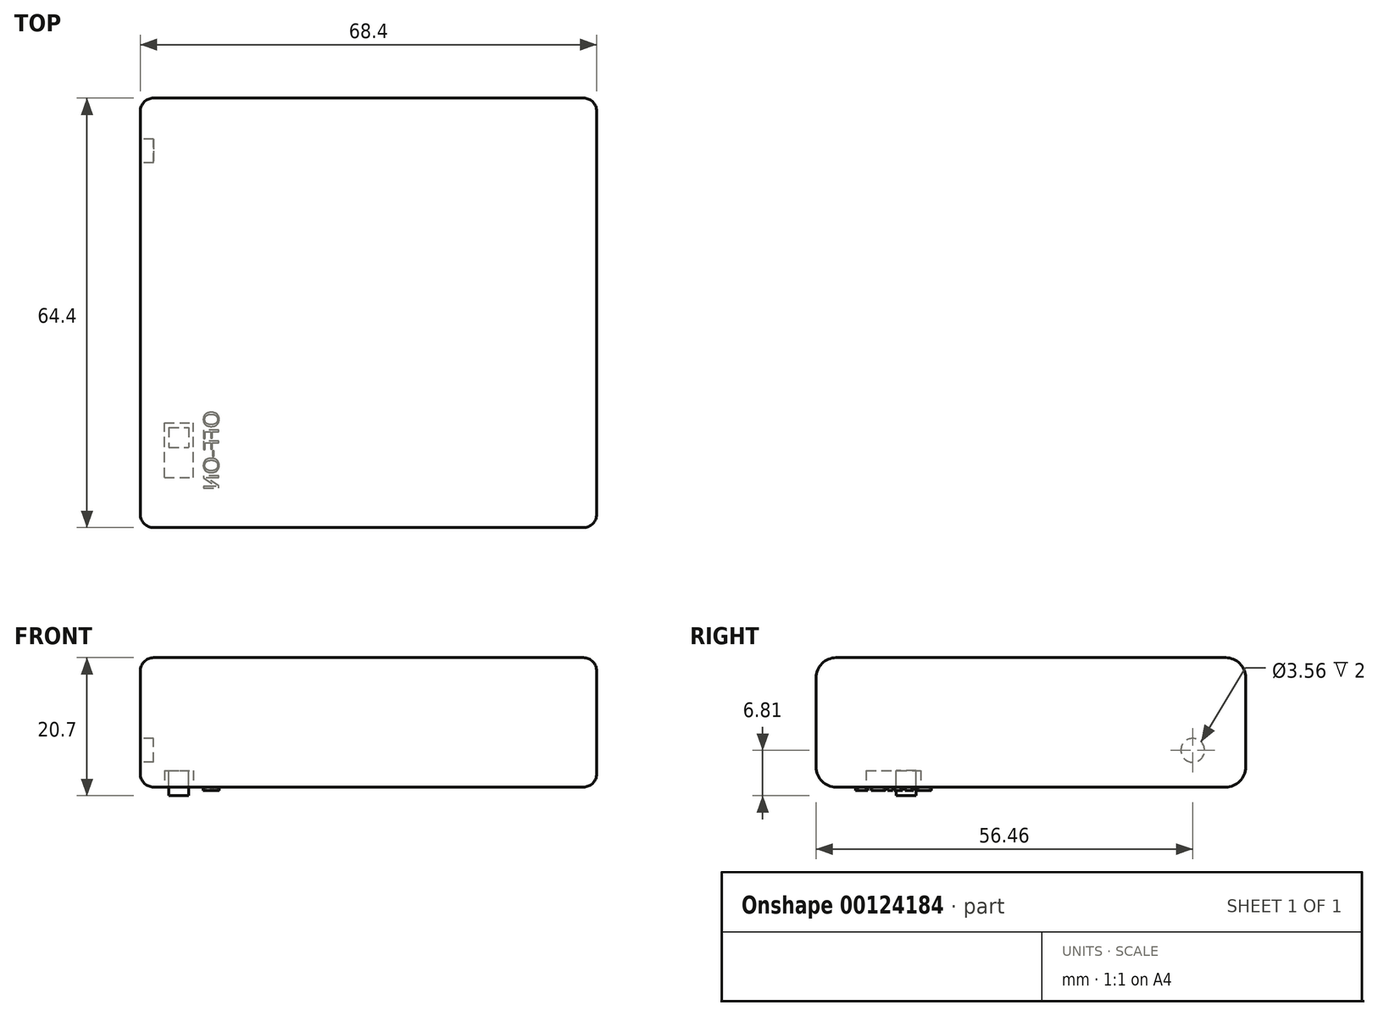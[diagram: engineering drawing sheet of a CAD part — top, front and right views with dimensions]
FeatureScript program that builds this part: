
annotation { "Feature Type Name" : "Feature", "Feature Type Description" : "" }
export const myFeature = defineFeature(function(context is Context, id is Id, definition is map)
    precondition{}
    {
        {
            var Q0;
            Q0=qCreatedBy(makeId("Top.planeOp"),FACE);
            var sketch = newSketch(context, id + "F0", { "sketchPlane" : qUnion([Q0])});
            skLineSegment(sketch, "E0.bottom", {"start": v(32.2, 34.2) * mm, "end": v(-32.2, 34.2) * mm});
            skLineSegment(sketch, "E0.top", {"start": v(32.2, -34.2) * mm, "end": v(-32.2, -34.2) * mm});
            skLineSegment(sketch, "E0.left", {"start": v(32.2, 34.2) * mm, "end": v(32.2, -34.2) * mm});
            skLineSegment(sketch, "E0.right", {"start": v(-32.2, 34.2) * mm, "end": v(-32.2, -34.2) * mm});
            skPoint(sketch, "E0.middle", {"position": v(0, 0) * mm});
            skSolve(sketch);
        }
        {
            var Q0;
            Q0 = qSketchRegion(id + "F0", true);
            extrude(context, id + "F1", {"entities" : qUnion([Q0]), "depth" : 19.4 * mm});
        }
        {
            var Q0;
            Q0=makeQuery(id+"F1.opExtrude","CAP_EDGE",EDGE,{"disambiguationData":[OSD([sQuery(id+"F0.wireOp",EDGE,"E0.right")])],"isStart":false});
            var Q1;
            Q1=makeQuery(id+"F1.opExtrude","CAP_EDGE",EDGE,{"disambiguationData":[OSD([sQuery(id+"F0.wireOp",EDGE,"E0.left")])],"isStart":false});
            var Q2;
            Q2=makeQuery(id+"F1.opExtrude","CAP_EDGE",EDGE,{"disambiguationData":[OSD([sQuery(id+"F0.wireOp",EDGE,"E0.left")])],"isStart":true});
            var Q3;
            Q3=makeQuery(id+"F1.opExtrude","CAP_EDGE",EDGE,{"disambiguationData":[OSD([sQuery(id+"F0.wireOp",EDGE,"E0.right")])],"isStart":true});
            fillet(context, id + "F2", {"entities" : qUnion([Q0, Q1, Q2, Q3]), "radius" : 3 * mm, "tangentPropagation" : true, "allowEdgeOverflow" : false});
        }
        {
            var Q0;
            Q0=makeQuery(id+"F1.opExtrude","SWEPT_FACE",FACE,{"disambiguationData":[OSD([sQuery(id+"F0.wireOp",EDGE,"E0.top")])]});
            var Q1;
            Q1=makeQuery(id+"F1.opExtrude","SWEPT_FACE",FACE,{"disambiguationData":[OSD([sQuery(id+"F0.wireOp",EDGE,"E0.bottom")])]});
            fillet(context, id + "F3", {"entities" : qUnion([Q0, Q1]), "radius" : 2 * mm, "tangentPropagation" : true, "allowEdgeOverflow" : false});
        }
        {
            var Q0;
            Q0=makeQuery(id+"F1.opExtrude","CAP_FACE",FACE,{"disambiguationData":[OSD([sQuery(id+"F0.wireOp",EDGE,"E0.bottom"),sQuery(id+"F0.wireOp",EDGE,"E0.top"),sQuery(id+"F0.wireOp",EDGE,"E0.left"),sQuery(id+"F0.wireOp",EDGE,"E0.right")])],"isStart":false});
            var sketch = newSketch(context, id + "F4", { "sketchPlane" : qUnion([Q0])});
            skLineSegment(sketch, "E1.bottom", {"start": v(24.7, 30.6) * mm, "end": v(16.5, 30.6) * mm});
            skLineSegment(sketch, "E1.top", {"start": v(24.7, 26.25) * mm, "end": v(16.5, 26.25) * mm});
            skLineSegment(sketch, "E1.left", {"start": v(24.7, 30.6) * mm, "end": v(24.7, 26.25) * mm});
            skLineSegment(sketch, "E1.right", {"start": v(16.5, 30.6) * mm, "end": v(16.5, 26.25) * mm});
            skSolve(sketch);
        }
        {
            var Q0;
            Q0 = qSketchRegion(id + "F4", true);
            extrude(context, id + "F5", {"entities" : qUnion([Q0]), "operationType" : NewBodyOperationType.REMOVE, "oppositeDirection" : true, "depth" : 2.5 * mm});
        }
        {
            var Q0;
            Q0=makeQuery(id+"F5.boolean.opBoolean","COPY",FACE,{"derivedFrom":makeQuery(id+"F5.opExtrude","CAP_FACE",FACE,{"disambiguationData":[OSD([sQuery(id+"F4.wireOp",EDGE,"E1.bottom"),sQuery(id+"F4.wireOp",EDGE,"E1.top"),sQuery(id+"F4.wireOp",EDGE,"E1.left"),sQuery(id+"F4.wireOp",EDGE,"E1.right")])],"isStart":false})});
            var sketch = newSketch(context, id + "F6", { "sketchPlane" : qUnion([Q0])});
            skLineSegment(sketch, "E2", {"start": v(16.5, 28.43) * mm, "end": v(24.7, 28.43) * mm, "construction": true});
            skLineSegment(sketch, "E3.bottom", {"start": v(17.18, 29.92) * mm, "end": v(20.18, 29.92) * mm});
            skLineSegment(sketch, "E3.top", {"start": v(17.18, 26.92) * mm, "end": v(20.18, 26.92) * mm});
            skLineSegment(sketch, "E3.left", {"start": v(17.18, 29.92) * mm, "end": v(17.18, 26.92) * mm});
            skLineSegment(sketch, "E3.right", {"start": v(20.18, 29.92) * mm, "end": v(20.18, 26.92) * mm});
            skPoint(sketch, "E3.middle", {"position": v(18.68, 28.42) * mm});
            skSolve(sketch);
        }
        {
            var Q0;
            Q0 = qSketchRegion(id + "F6", true);
            extrude(context, id + "F7", {"entities" : qUnion([Q0]), "operationType" : NewBodyOperationType.ADD, "depth" : (1.3 + 2.5) * mm});
        }
        {
            var Q0;
            Q0=makeQuery(id+"F1.opExtrude","SWEPT_FACE",FACE,{"disambiguationData":[OSD([sQuery(id+"F0.wireOp",EDGE,"E0.bottom")])]});
            var sketch = newSketch(context, id + "F8", { "sketchPlane" : qUnion([Q0])});
            skCircle(sketch, "E4", {"center": v(24.26, 13.89) * mm, "radius": 1.78 * mm});
            skSolve(sketch);
        }
        {
            var Q0;
            Q0 = qSketchRegion(id + "F8", true);
            extrude(context, id + "F9", {"entities" : qUnion([Q0]), "operationType" : NewBodyOperationType.REMOVE, "oppositeDirection" : true, "depth" : 2 * mm});
        }
        {
            var Q0;
            Q0=makeQuery(id+"F1.opExtrude","CAP_FACE",FACE,{"disambiguationData":[OSD([sQuery(id+"F0.wireOp",EDGE,"E0.bottom"),sQuery(id+"F0.wireOp",EDGE,"E0.top"),sQuery(id+"F0.wireOp",EDGE,"E0.left"),sQuery(id+"F0.wireOp",EDGE,"E0.right")])],"isStart":false});
            var sketch = newSketch(context, id + "F10", { "sketchPlane" : qUnion([Q0])});
            skText(sketch, "E5", { "text": "OFF-ON", "fontName": "OpenSans-Regular.ttf"});
            skPoint(sketch, "E6", {"position": v(20.6, 26.25) * mm});
            const initialGuessF10  = {"E5": [0.01472, 0.02242, 1, 0, 0.00233]};
            skSetInitialGuess(sketch, initialGuessF10);
            skSolve(sketch);
        }
        {
            var Q0;
            Q0 = qSketchRegion(id + "F10", true);
            extrude(context, id + "F11", {"entities" : qUnion([Q0]), "operationType" : NewBodyOperationType.ADD, "depth" : 0.5 * mm});
        }
        {
            var Q0;
            Q0=makeQuery(id+"F1.opExtrude","CAP_FACE",FACE,{"disambiguationData":[OSD([sQuery(id+"F0.wireOp",EDGE,"E0.bottom"),sQuery(id+"F0.wireOp",EDGE,"E0.top"),sQuery(id+"F0.wireOp",EDGE,"E0.left"),sQuery(id+"F0.wireOp",EDGE,"E0.right")])],"isStart":true});
            var sketch = newSketch(context, id + "F12", { "sketchPlane" : qUnion([Q0])});
            skCircle(sketch, "E7", {"center": v(0, -28.33) * mm, "radius": 2.33 * mm});
            skSolve(sketch);
        }
        {
            var Q0;
            Q0=qCreatedBy(makeId("Top.planeOp"),FACE);
            var sketch = newSketch(context, id + "F13", { "sketchPlane" : qUnion([Q0])});
            skLineSegment(sketch, "E8", {"start": v(0, 61.28) * mm, "end": v(0, -59.76) * mm, "construction": true});
            skSolve(sketch);
        }
        {
            var Q0;
            Q0=makeQuery(id+"F1.opExtrude","SWEPT_BODY",BODY,{"disambiguationData":[OSD([sQuery(id+"F0.wireOp",EDGE,"E0.bottom"),sQuery(id+"F0.wireOp",EDGE,"E0.top"),sQuery(id+"F0.wireOp",EDGE,"E0.left"),sQuery(id+"F0.wireOp",EDGE,"E0.right")])]});
            var Q1;
            Q1=sQuery(id+"F13.wireOp",EDGE,"E8");
            transform(context, id + "F14", {"entities" : qUnion([Q0]), "transformType" : TransformType.ROTATION, "transformAxis" : qUnion([Q1]), "angle" : 180 * degree, "makeCopy" : false});
        }
        {
            var Q0;
            Q0=qCreatedBy(makeId("Right.planeOp"),FACE);
            var sketch = newSketch(context, id + "F15", { "sketchPlane" : qUnion([Q0])});
            skLineSegment(sketch, "E9", {"start": v(0, 0) * mm, "end": v(0, 39) * mm, "construction": true});
            skSolve(sketch);
        }
        {
            var Q0;
            Q0=makeQuery(id+"F1.opExtrude","SWEPT_BODY",BODY,{"disambiguationData":[OSD([sQuery(id+"F0.wireOp",EDGE,"E0.bottom"),sQuery(id+"F0.wireOp",EDGE,"E0.top"),sQuery(id+"F0.wireOp",EDGE,"E0.left"),sQuery(id+"F0.wireOp",EDGE,"E0.right")])]});
            var Q1;
            Q1=sQuery(id+"F15.wireOp",EDGE,"E9");
            transform(context, id + "F16", {"entities" : qUnion([Q0]), "transformType" : TransformType.ROTATION, "transformAxis" : qUnion([Q1]), "angle" : 90 * degree, "makeCopy" : false});
        }
    });
